# Revit family: SELECTABLE MAGIC CYLINDER LIGHT_30W
name_source: partatom
category: Lighting Fixtures
units: mm (PartAtom-declared; Revit-internal decimal feet)

## family parameters
Cut with Voids When Loaded = No
Host = Face
Light Source = No
Part Type = Normal
Room Calculation Point = No
Round Connector Dimension = Use Diameter
Shared = No

## types (48) — shared parameters
Apparent Load = 0 VA
Average life based on 104F(HRS) = 50000
BASE HEIGHT_1 = 0' - 2 5/8"
BOTTOM LENGTH = 0' - 3 31/32"
BOTTOM LENGTH 1 = 0' - 0 3/16"
BOTTOM WIDTH = 0' - 1 5/8"
BOTTOM WIDTH 1 = 0' - 0 3/16"
Base Rod Pr1 = 0' - 0 1/4"
CRI = 90
Canopy Dia = 0' - 3 21/32"
Canopy Height = 0' - 0 3/16"
Default Elevation = 4' - 0"
Description = This architectural Magic Cylinder Light is designed for accent lighting and features a state-of-the-art design.
Dimming/Control1 = Triac dimming
Finish/Color = BLACK
GLASS = Glass
GLASS OFFSET = 0' - 4"
GLASS THICKNESS = 0' - 0 1/8"
IP Rating = 20
LENGTH = 0' - 2 3/4"
LIGHT VERTYCAL ALIGMNENT = 0' - 0 1/2"
Load Classification = Lighting
Manufacturer = Above All Lighting
Power Factor = 1
REFERANCE = No
TILT ANGLE = 0.00°
TRACK PENDENT MOUNT = No
Type Comments = SELECTABLE MAGIC CYLINDER LIGHT
URL = https://www.abovealllighting.com
Voltage = 120 V
X OFFSET = 0' - 0"
Y OFFSET = 0' - 0"

## per-type parameters (varying)
| type | BASE HEIGHT | BEAMING ANGLE | FIXED END HEIGHT | FIXED END HEIGHT 1 | GLASS RADIUS | H TYPE TRACK MOUNT | INITIAL INTENSITY | J TYPE TRACK MOUNT | LIGHT DIA | LIGHT LENGTH | LIGHT RADIUS | Order number | Pendent Mount | Pendent Surface Mount Base | Rod Mounted | Surface Mount | Surface Mount Base |
| SMCL-25SP-SW904-15-HTMK-MBK | 0' - 2 5/8" | 15.00° | 0' - 6" | 0' - 6" | 0' - 1 11/32" | Yes | 1700 lm | No | 0' - 2 3/4" | 0' - 5 5/16" | 0' - 1 3/8" | 17843 | No | No | Yes | No | No |
| SMCL-25SP-SW904-24-HTMK-MBK | 0' - 2 5/8" | 24.00° | 0' - 6" | 0' - 6" | 0' - 1 11/32" | Yes | 1700 lm | No | 0' - 2 3/4" | 0' - 5 5/16" | 0' - 1 3/8" | 17844 | No | No | Yes | No | No |
| SMCL-25SP-SW904-36-HTMK-MBK | 0' - 2 5/8" | 36.00° | 0' - 6" | 0' - 6" | 0' - 1 11/32" | Yes | 1700 lm | No | 0' - 2 3/4" | 0' - 5 5/16" | 0' - 1 3/8" | 17845 | No | No | Yes | No | No |
| SMCL-25SP-SW904-50-HTMK-MBK | 0' - 2 5/8" | 50.00° | 0' - 6" | 0' - 6" | 0' - 1 11/32" | Yes | 1400 lm | No | 0' - 2 3/4" | 0' - 5 5/16" | 0' - 1 3/8" | 17846 | No | No | Yes | No | No |
| SMCL-35SP-SW904-15-HTMK-MBK | 0' - 2 5/8" | 15.00° | 0' - 6" | 0' - 6" | 0' - 1 17/32" | Yes | 2800 lm | No | 0' - 3 5/32" | 0' - 6 5/16" | 0' - 1 9/16" | 17847 | No | No | Yes | No | No |
| SMCL-35SP-SW904-24-HTMK-MBK | 0' - 2 5/8" | 24.00° | 0' - 6" | 0' - 6" | 0' - 1 17/32" | Yes | 2800 lm | No | 0' - 3 5/32" | 0' - 6 5/16" | 0' - 1 9/16" | 17848 | No | No | Yes | No | No |
| SMCL-35SP-SW904-36-HTMK-MBK | 0' - 2 5/8" | 36.00° | 0' - 6" | 0' - 6" | 0' - 1 17/32" | Yes | 2800 lm | No | 0' - 3 5/32" | 0' - 6 5/16" | 0' - 1 9/16" | 17849 | No | No | Yes | No | No |
| SMCL-35SP-SW904-50-HTMK-MBK | 0' - 2 5/8" | 50.00° | 0' - 6" | 0' - 6" | 0' - 1 17/32" | Yes | 2200 lm | No | 0' - 3 5/32" | 0' - 6 5/16" | 0' - 1 9/16" | 17850 | No | No | Yes | No | No |
| SMCL-25SP-SW904-15-JTMK-MBK | 0' - 2 5/8" | 15.00° | 0' - 6" | 0' - 6" | 0' - 1 11/32" | No | 1700 lm | Yes | 0' - 2 3/4" | 0' - 5 5/16" | 0' - 1 3/8" | 17855 | No | No | Yes | No | No |
| SMCL-25SP-SW904-24-JTMK-MBK | 0' - 2 5/8" | 24.00° | 0' - 6" | 0' - 6" | 0' - 1 11/32" | No | 1700 lm | Yes | 0' - 2 3/4" | 0' - 5 5/16" | 0' - 1 3/8" | 17856 | No | No | Yes | No | No |
| SMCL-25SP-SW904-36-JTMK-MBK | 0' - 2 5/8" | 36.00° | 0' - 6" | 0' - 6" | 0' - 1 11/32" | No | 1700 lm | Yes | 0' - 2 3/4" | 0' - 5 5/16" | 0' - 1 3/8" | 17857 | No | No | Yes | No | No |
| SMCL-25SP-SW904-50-JTMK-MBK | 0' - 2 5/8" | 50.00° | 0' - 6" | 0' - 6" | 0' - 1 11/32" | No | 1400 lm | Yes | 0' - 2 3/4" | 0' - 5 5/16" | 0' - 1 3/8" | 17858 | No | No | Yes | No | No |
| SMCL-35SP-SW904-15-JTMK-MBK | 0' - 2 5/8" | 15.00° | 0' - 6" | 0' - 6" | 0' - 1 17/32" | No | 2800 lm | Yes | 0' - 3 5/32" | 0' - 6 5/16" | 0' - 1 9/16" | 17859 | No | No | Yes | No | No |
| SMCL-35SP-SW904-24-JTMK-MBK | 0' - 2 5/8" | 24.00° | 0' - 6" | 0' - 6" | 0' - 1 17/32" | No | 2800 lm | Yes | 0' - 3 5/32" | 0' - 6 5/16" | 0' - 1 9/16" | 17860 | No | No | Yes | No | No |
| SMCL-35SP-SW904-36-JTMK-MBK | 0' - 2 5/8" | 36.00° | 0' - 6" | 0' - 6" | 0' - 1 17/32" | No | 2800 lm | Yes | 0' - 3 5/32" | 0' - 6 5/16" | 0' - 1 9/16" | 17861 | No | No | Yes | No | No |
| SMCL-35SP-SW904-50-JTMK-MBK | 0' - 2 5/8" | 50.00° | 0' - 6" | 0' - 6" | 0' - 1 17/32" | No | 2200 lm | Yes | 0' - 3 5/32" | 0' - 6 5/16" | 0' - 1 9/16" | 17862 | No | No | Yes | No | No |
| SMCL-25SP-SW904-15-PMK-MBK | 0' - 0 3/16" | 15.00° | 1' - 11 5/8" | 1' - 11 5/8" | 0' - 1 11/32" | No | 1700 lm | No | 0' - 2 3/4" | 0' - 5 5/16" | 0' - 1 3/8" | 17819 | Yes | Yes | No | No | No |
| SMCL-25SP-SW904-24-PMK-MBK | 0' - 0 3/16" | 24.00° | 1' - 11 5/8" | 1' - 11 5/8" | 0' - 1 11/32" | No | 1700 lm | No | 0' - 2 3/4" | 0' - 5 5/16" | 0' - 1 3/8" | 17820 | Yes | Yes | No | No | No |
| SMCL-25SP-SW904-36-PMK-MBK | 0' - 0 3/16" | 36.00° | 1' - 11 5/8" | 1' - 11 5/8" | 0' - 1 11/32" | No | 1700 lm | No | 0' - 2 3/4" | 0' - 5 5/16" | 0' - 1 3/8" | 17821 | Yes | Yes | No | No | No |
| SMCL-25SP-SW904-50-PMK-MBK | 0' - 0 3/16" | 50.00° | 1' - 11 5/8" | 1' - 11 5/8" | 0' - 1 11/32" | No | 1400 lm | No | 0' - 2 3/4" | 0' - 5 5/16" | 0' - 1 3/8" | 17822 | Yes | Yes | No | No | No |
| SMCL-35SP-SW904-15-PMK-MBK | 0' - 0 3/16" | 15.00° | 1' - 11 5/8" | 1' - 11 5/8" | 0' - 1 17/32" | No | 2800 lm | No | 0' - 3 5/32" | 0' - 6 5/16" | 0' - 1 9/16" | 17823 | Yes | Yes | No | No | No |
| SMCL-35SP-SW904-24-PMK-MBK | 0' - 0 3/16" | 24.00° | 1' - 11 5/8" | 1' - 11 5/8" | 0' - 1 17/32" | No | 2800 lm | No | 0' - 3 5/32" | 0' - 6 5/16" | 0' - 1 9/16" | 17824 | Yes | Yes | No | No | No |
| SMCL-35SP-SW904-36-PMK-MBK | 0' - 0 3/16" | 36.00° | 1' - 11 5/8" | 1' - 11 5/8" | 0' - 1 17/32" | No | 2800 lm | No | 0' - 3 5/32" | 0' - 6 5/16" | 0' - 1 9/16" | 17825 | Yes | Yes | No | No | No |
| SMCL-35SP-SW904-50-PMK-MBK | 0' - 0 3/16" | 50.00° | 1' - 11 5/8" | 1' - 11 5/8" | 0' - 1 17/32" | No | 2200 lm | No | 0' - 3 5/32" | 0' - 6 5/16" | 0' - 1 9/16" | 17826 | Yes | Yes | No | No | No |
| SMCL-25SP-SW904-15-SMK-MBK | 0' - 0 3/16" | 15.00° | 0' - 6" | 0' - 6" | 0' - 1 11/32" | No | 1700 lm | No | 0' - 2 3/4" | 0' - 5 5/16" | 0' - 1 3/8" | 17831 | No | No | No | Yes | Yes |
| SMCL-25SP-SW904-24-SMK-MBK | 0' - 0 3/16" | 24.00° | 0' - 6" | 0' - 6" | 0' - 1 11/32" | No | 1700 lm | No | 0' - 2 3/4" | 0' - 5 5/16" | 0' - 1 3/8" | 17832 | No | No | No | Yes | Yes |
| SMCL-25SP-SW904-36-SMK-MBK | 0' - 0 3/16" | 36.00° | 0' - 6" | 0' - 6" | 0' - 1 11/32" | No | 1700 lm | No | 0' - 2 3/4" | 0' - 5 5/16" | 0' - 1 3/8" | 17833 | No | No | No | Yes | Yes |
| SMCL-25SP-SW904-50-SMK-MBK | 0' - 0 3/16" | 50.00° | 0' - 6" | 0' - 6" | 0' - 1 11/32" | No | 1400 lm | No | 0' - 2 3/4" | 0' - 5 5/16" | 0' - 1 3/8" | 17834 | No | No | No | Yes | Yes |
| SMCL-35SP-SW904-15-SMK-MBK | 0' - 0 3/16" | 15.00° | 0' - 6" | 0' - 6" | 0' - 1 17/32" | No | 2800 lm | No | 0' - 3 5/32" | 0' - 6 5/16" | 0' - 1 9/16" | 17835 | No | No | No | Yes | Yes |
| SMCL-35SP-SW904-24-SMK-MBK | 0' - 0 3/16" | 24.00° | 0' - 6" | 0' - 6" | 0' - 1 17/32" | No | 2800 lm | No | 0' - 3 5/32" | 0' - 6 5/16" | 0' - 1 9/16" | 17836 | No | No | No | Yes | Yes |
| SMCL-35SP-SW904-36-SMK-MBK | 0' - 0 3/16" | 36.00° | 0' - 6" | 0' - 6" | 0' - 1 17/32" | No | 2800 lm | No | 0' - 3 5/32" | 0' - 6 5/16" | 0' - 1 9/16" | 17837 | No | No | No | Yes | Yes |
| SMCL-35SP-SW904-50-SMK-MBK | 0' - 0 3/16" | 50.00° | 0' - 6" | 0' - 6" | 0' - 1 17/32" | No | 2200 lm | No | 0' - 3 5/32" | 0' - 6 5/16" | 0' - 1 9/16" | 17838 | No | No | No | Yes | Yes |
| SMCL-25SP-SW904-15-HTPMK-MBK | 0' - 2 5/8" | 15.00° | 1' - 11 5/8" | 1' - 11 5/8" | 0' - 1 11/32" | No | 1700 lm | No | 0' - 2 3/4" | 0' - 5 5/16" | 0' - 1 3/8" | 17867 | Yes | No | Yes | No | No |
| SMCL-25SP-SW904-24-HTPMK-MBK | 0' - 2 5/8" | 24.00° | 1' - 11 5/8" | 1' - 11 5/8" | 0' - 1 11/32" | No | 1700 lm | No | 0' - 2 3/4" | 0' - 5 5/16" | 0' - 1 3/8" | 17868 | Yes | No | Yes | No | No |
| SMCL-25SP-SW904-36-HTPMK-MBK | 0' - 2 5/8" | 36.00° | 1' - 11 5/8" | 1' - 11 5/8" | 0' - 1 11/32" | No | 1700 lm | No | 0' - 2 3/4" | 0' - 5 5/16" | 0' - 1 3/8" | 17869 | Yes | No | Yes | No | No |
| SMCL-25SP-SW904-50-HTPMK-MBK | 0' - 2 5/8" | 50.00° | 1' - 11 5/8" | 1' - 11 5/8" | 0' - 1 11/32" | No | 1400 lm | No | 0' - 2 3/4" | 0' - 5 5/16" | 0' - 1 3/8" | 17870 | Yes | No | Yes | No | No |
| SMCL-35SP-SW904-15-HTPMK-MBK | 0' - 2 5/8" | 15.00° | 1' - 11 5/8" | 1' - 11 5/8" | 0' - 1 17/32" | No | 2800 lm | No | 0' - 3 5/32" | 0' - 6 5/16" | 0' - 1 9/16" | 17871 | Yes | No | Yes | No | No |
| SMCL-35SP-SW904-24-HTPMK-MBK | 0' - 2 5/8" | 24.00° | 1' - 11 5/8" | 1' - 11 5/8" | 0' - 1 17/32" | No | 2800 lm | No | 0' - 3 5/32" | 0' - 6 5/16" | 0' - 1 9/16" | 17872 | Yes | No | Yes | No | No |
| SMCL-35SP-SW904-24-JTPMK-MBK | 0' - 2 5/8" | 24.00° | 1' - 11 5/8" | 1' - 11 5/8" | 0' - 1 17/32" | No | 2800 lm | No | 0' - 3 5/32" | 0' - 6 5/16" | 0' - 1 9/16" | 17884 | Yes | No | Yes | No | No |
| SMCL-35SP-SW904-36-HTPMK-MBK | 0' - 2 5/8" | 36.00° | 1' - 11 5/8" | 1' - 11 5/8" | 0' - 1 17/32" | No | 2800 lm | No | 0' - 3 5/32" | 0' - 6 5/16" | 0' - 1 9/16" | 17873 | Yes | No | Yes | No | No |
| SMCL-35SP-SW904-36-JTPMK-MBK | 0' - 2 5/8" | 36.00° | 1' - 11 5/8" | 1' - 11 5/8" | 0' - 1 17/32" | No | 2800 lm | No | 0' - 3 5/32" | 0' - 6 5/16" | 0' - 1 9/16" | 17885 | Yes | No | Yes | No | No |
| SMCL-35SP-SW904-50-HTPMK-MBK | 0' - 2 5/8" | 50.00° | 1' - 11 5/8" | 1' - 11 5/8" | 0' - 1 17/32" | No | 2200 lm | No | 0' - 3 5/32" | 0' - 6 5/16" | 0' - 1 9/16" | 17874 | Yes | No | Yes | No | No |
| SMCL-35SP-SW904-50-JTPMK-MBK | 0' - 2 5/8" | 50.00° | 1' - 11 5/8" | 1' - 11 5/8" | 0' - 1 17/32" | No | 2200 lm | No | 0' - 3 5/32" | 0' - 6 5/16" | 0' - 1 9/16" | 17886 | Yes | No | Yes | No | No |
| SMCL-35SP-SW904-15-JTPMK-MBK | 0' - 2 5/8" | 15.00° | 1' - 11 5/8" | 1' - 11 5/8" | 0' - 1 17/32" | No | 2800 lm | No | 0' - 3 5/32" | 0' - 6 5/16" | 0' - 1 9/16" | 17883 | Yes | No | Yes | No | No |
| SMCL-25SP-SW904-15-JTPMK-MBK | 0' - 2 5/8" | 15.00° | 1' - 11 5/8" | 1' - 11 5/8" | 0' - 1 11/32" | No | 1700 lm | No | 0' - 2 3/4" | 0' - 5 5/16" | 0' - 1 3/8" | 17879 | Yes | No | Yes | No | No |
| SMCL-25SP-SW904-24-JTPMK-MBK | 0' - 2 5/8" | 24.00° | 1' - 11 5/8" | 1' - 11 5/8" | 0' - 1 11/32" | No | 1700 lm | No | 0' - 2 3/4" | 0' - 5 5/16" | 0' - 1 3/8" | 17880 | Yes | No | Yes | No | No |
| SMCL-25SP-SW904-36-JTPMK-MBK | 0' - 2 5/8" | 36.00° | 1' - 11 5/8" | 1' - 11 5/8" | 0' - 1 11/32" | No | 1700 lm | No | 0' - 2 3/4" | 0' - 5 5/16" | 0' - 1 3/8" | 17881 | Yes | No | Yes | No | No |
| SMCL-25SP-SW904-50-JTPMK-MBK | 0' - 2 5/8" | 50.00° | 1' - 11 5/8" | 1' - 11 5/8" | 0' - 1 11/32" | No | 1400 lm | No | 0' - 2 3/4" | 0' - 5 5/16" | 0' - 1 3/8" | 17882 | Yes | No | Yes | No | No |

note: column(s) folded — value = type name in every type: Model

## geometry (parser evidence)
native form markers: Sweep x97
no freeform markers — native parametric forms only
